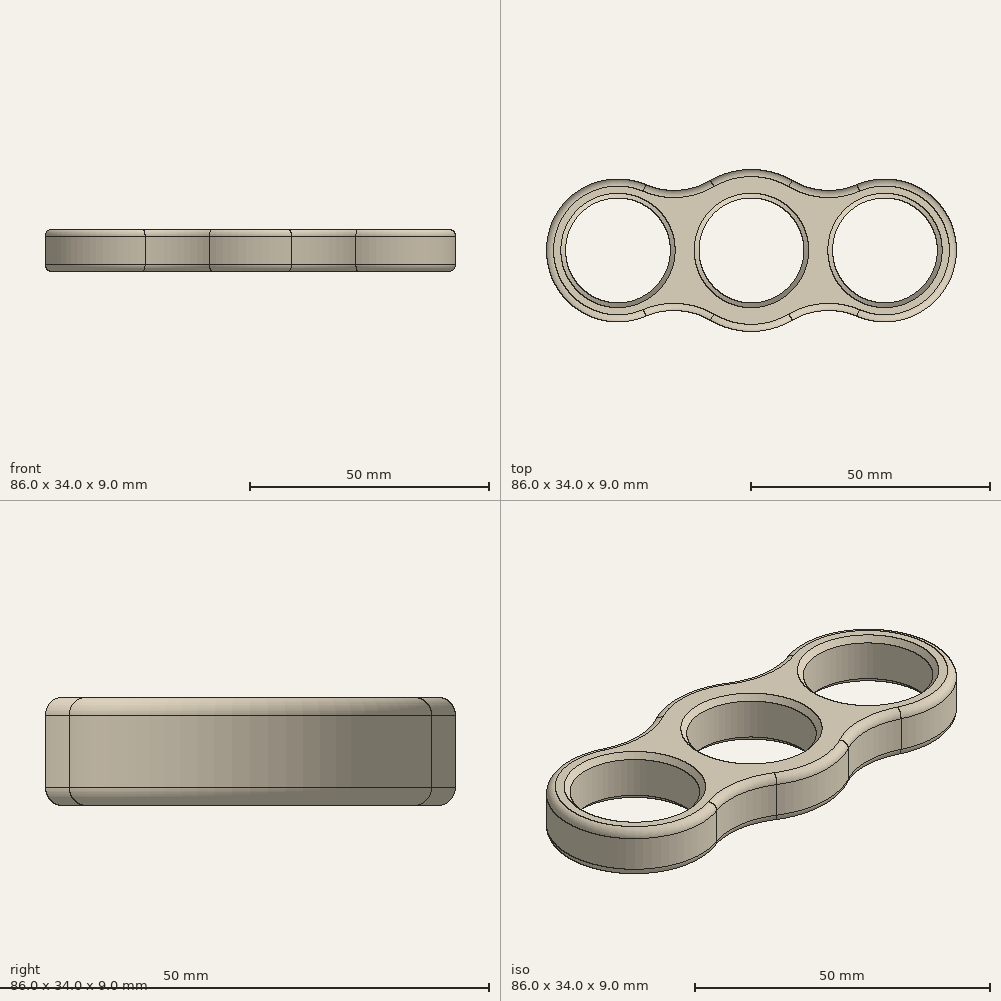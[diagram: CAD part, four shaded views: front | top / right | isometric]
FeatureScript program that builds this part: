
annotation { "Feature Type Name" : "Feature", "Feature Type Description" : "" }
export const myFeature = defineFeature(function(context is Context, id is Id, definition is map)
    precondition{}
    {
        {
            var Q0;
            Q0=qCreatedBy(makeId("Top.planeOp"),FACE);
            var sketch = newSketch(context, id + "F0", { "sketchPlane" : qUnion([Q0])});
            skCircle(sketch, "E0", {"center": v(0, 0) * mm, "radius": 11 * mm});
            skCircle(sketch, "E1", {"center": v(28, 0) * mm, "radius": 11 * mm});
            skCircle(sketch, "E2", {"center": v(-28, 0) * mm, "radius": 11 * mm});
            skArc(sketch, "E3", {"start": v(-22.1, 13.8) * mm, "mid": v(-43, 0) * mm, "end": v(-22.1, -13.8) * mm});
            skArc(sketch, "E4", {"start": v(22.1, 13.8) * mm, "mid": v(43, 0) * mm, "end": v(22.1, -13.8) * mm});
            skArc(sketch, "E5", {"start": v(-8.61, 14.66) * mm, "mid": v(0, 17) * mm, "end": v(8.61, 14.66) * mm});
            skArc(sketch, "E6", {"start": v(-8.61, -14.66) * mm, "mid": v(0, -17) * mm, "end": v(8.61, -14.66) * mm});
            skArc(sketch, "E7", {"start": v(8.61, 14.66) * mm, "mid": v(15.26, 12.62) * mm, "end": v(22.1, 13.8) * mm});
            skArc(sketch, "E8", {"start": v(-22.1, 13.8) * mm, "mid": v(-15.26, 12.62) * mm, "end": v(-8.61, 14.66) * mm});
            skArc(sketch, "E9", {"start": v(-22.1, -13.8) * mm, "mid": v(-15.26, -12.62) * mm, "end": v(-8.61, -14.66) * mm});
            skArc(sketch, "E10", {"start": v(8.61, -14.66) * mm, "mid": v(15.26, -12.62) * mm, "end": v(22.1, -13.8) * mm});
            skSolve(sketch);
        }
        {
            var Q0;
            Q0=makeQuery(id+"F0.imprint","IMPRINT",FACE,{"disambiguationData":[TD([[makeQuery(id+"F0.imprint","IMPRINT",EDGE,{"derivedFrom":sQuery(id+"F0.wireOp",EDGE,"E0")}),-1.0]])]});
            extrude(context, id + "F1", {"entities" : qUnion([Q0]), "depth" : 9 * mm});
        }
        {
            var Q0;
            Q0=makeQuery(id+"F1.opExtrude","CAP_EDGE",EDGE,{"disambiguationData":[OSD([sQuery(id+"F0.wireOp",EDGE,"E5")])],"isStart":true});
            var Q1;
            Q1=makeQuery(id+"F1.opExtrude","CAP_EDGE",EDGE,{"disambiguationData":[OSD([sQuery(id+"F0.wireOp",EDGE,"E5")])],"isStart":false});
            fillet(context, id + "F2", {"entities" : qUnion([Q0, Q1]), "radius" : 1.5 * mm, "tangentPropagation" : true, "allowEdgeOverflow" : false});
        }
        {
            var Q0;
            Q0=makeQuery(id+"F1.opExtrude","SWEPT_FACE",FACE,{"disambiguationData":[OSD([sQuery(id+"F0.wireOp",EDGE,"E2")])]});
            var Q1;
            Q1=makeQuery(id+"F1.opExtrude","SWEPT_FACE",FACE,{"disambiguationData":[OSD([sQuery(id+"F0.wireOp",EDGE,"E0")])]});
            var Q2;
            Q2=makeQuery(id+"F1.opExtrude","SWEPT_FACE",FACE,{"disambiguationData":[OSD([sQuery(id+"F0.wireOp",EDGE,"E1")])]});
            chamfer(context, id + "F3", {"entities" : qUnion([Q0, Q1, Q2]), "width" : 1 * mm, "tangentPropagation" : true});
        }
    });
